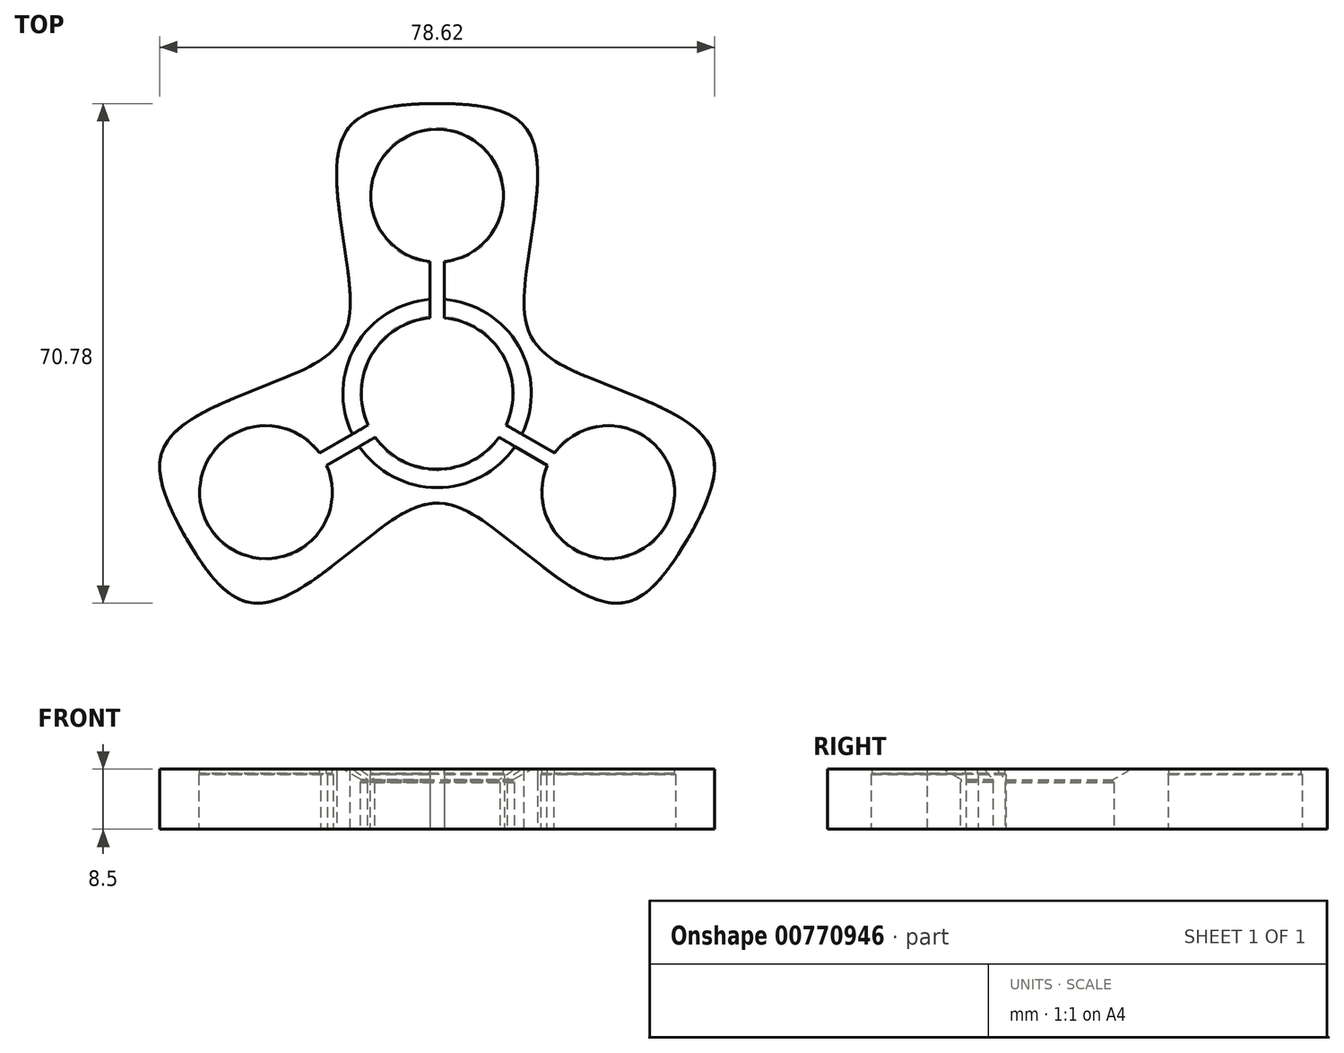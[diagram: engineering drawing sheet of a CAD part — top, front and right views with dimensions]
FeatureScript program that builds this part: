
annotation { "Feature Type Name" : "Feature", "Feature Type Description" : "" }
export const myFeature = defineFeature(function(context is Context, id is Id, definition is map)
    precondition{}
    {
        {
            var Q0;
            Q0=qCreatedBy(makeId("Top.planeOp"),FACE);
            var sketch = newSketch(context, id + "F0", { "sketchPlane" : qUnion([Q0])});
            skLineSegment(sketch, "E0", {"start": v(0, 0) * mm, "end": v(71.1, 41.05) * mm, "construction": true});
            skLineSegment(sketch, "E1", {"start": v(0, 0) * mm, "end": v(-71.1, 41.05) * mm, "construction": true});
            skCircle(sketch, "E2", {"center": v(0, 0) * mm, "radius": 10.9 * mm, "construction": true});
            skCircle(sketch, "E3", {"center": v(0, 28) * mm, "radius": 9.55 * mm});
            skLineSegment(sketch, "E4", {"start": v(-16, 41.05) * mm, "end": v(16, 41.05) * mm});
            skLineSegment(sketch, "E5", {"start": v(16, 41.05) * mm, "end": v(11.13, 6.43) * mm});
            skLineSegment(sketch, "E6", {"start": v(-16, 41.05) * mm, "end": v(-11.13, 6.43) * mm});
            skLineSegment(sketch, "E7", {"start": v(0, 28) * mm, "end": v(0, 41.05) * mm, "construction": true});
            skPoint(sketch, "E8", {"position": v(0, 37.55) * mm});
            skArc(sketch, "E9", {"start": v(9.44, 5.45) * mm, "mid": v(0, 10.9) * mm, "end": v(-9.44, 5.45) * mm});
            skLineSegment(sketch, "E10", {"start": v(-9.44, 5.45) * mm, "end": v(-11.13, 6.43) * mm});
            skLineSegment(sketch, "E11", {"start": v(9.44, 5.45) * mm, "end": v(11.13, 6.43) * mm});
            skSolve(sketch);
        }
        {
            var Q0;
            Q0=qSketchRegion(id+"F0",true);
            extrude(context, id + "F1", {"entities" : qUnion([Q0]), "endBound" : BoundingType.SYMMETRIC, "depth" : 7 * mm, "offsetDistance" : 25 * mm});
        }
        {
            var Q0;
            Q0=makeQuery(id+"F1.opExtrude","SWEPT_EDGE",EDGE,{"disambiguationData":[OSD([sQuery(id+"F0.wireOp",EDGE,"E4"),sQuery(id+"F0.wireOp",EDGE,"E6")])]});
            var Q1;
            Q1=makeQuery(id+"F1.opExtrude","SWEPT_EDGE",EDGE,{"disambiguationData":[OSD([sQuery(id+"F0.wireOp",EDGE,"E4"),sQuery(id+"F0.wireOp",EDGE,"E5")])]});
            fillet(context, id + "F2", {"entities" : qUnion([Q0, Q1]), "radius" : 14 * mm, "tangentPropagation" : true, "rho" : .6, "crossSection" : FilletCrossSection.CONIC, "allowEdgeOverflow" : false});
        }
        {
            var Q0;
            Q0=makeQuery(id+"F1.opExtrude","CAP_FACE",FACE,{"disambiguationData":[OSD([sQuery(id+"F0.wireOp",EDGE,"E3"),sQuery(id+"F0.wireOp",EDGE,"E4"),sQuery(id+"F0.wireOp",EDGE,"E5"),sQuery(id+"F0.wireOp",EDGE,"E6"),sQuery(id+"F0.wireOp",EDGE,"E9"),sQuery(id+"F0.wireOp",EDGE,"E10"),sQuery(id+"F0.wireOp",EDGE,"E11")])],"isStart":false});
            var sketch = newSketch(context, id + "F3", { "sketchPlane" : qUnion([Q0])});
            skCircle(sketch, "E12.0", {"center": v(0, 28) * mm, "radius": 9.55 * mm});
            skCircle(sketch, "E13.0", {"center": v(0, 28) * mm, "radius": 9.4 * mm});
            skArc(sketch, "E14.0", {"start": v(9.44, 5.45) * mm, "mid": v(0, 10.9) * mm, "end": v(-9.44, 5.45) * mm});
            skArc(sketch, "E15.0", {"start": v(9.3, 5.37) * mm, "mid": v(0, 10.75) * mm, "end": v(-9.3, 5.37) * mm});
            skLineSegment(sketch, "E16", {"start": v(-9.3, 5.37) * mm, "end": v(-9.44, 5.45) * mm});
            skLineSegment(sketch, "E17", {"start": v(9.3, 5.37) * mm, "end": v(9.44, 5.45) * mm});
            skSolve(sketch);
        }
        {
            var Q0;
            Q0=makeQuery(id+"F3.imprint","IMPRINT",FACE,{"disambiguationData":[TD([[makeQuery(id+"F3.imprint","IMPRINT",EDGE,{"derivedFrom":sQuery(id+"F3.wireOp",EDGE,"E14.0")}),1.0]])]});
            extrude(context, id + "F4", {"entities" : qUnion([Q0]), "operationType" : NewBodyOperationType.ADD, "oppositeDirection" : true, "depth" : .4 * mm, "offsetDistance" : 25 * mm});
        }
        {
            var Q0;
            Q0=makeQuery(id+"F4.boolean.opBoolean","MERGE",FACE,{"derivedFrom":[makeQuery(id+"F1.opExtrude","CAP_FACE",FACE,{"disambiguationData":[OSD([sQuery(id+"F0.wireOp",EDGE,"E3"),sQuery(id+"F0.wireOp",EDGE,"E4"),sQuery(id+"F0.wireOp",EDGE,"E5"),sQuery(id+"F0.wireOp",EDGE,"E6"),sQuery(id+"F0.wireOp",EDGE,"E9"),sQuery(id+"F0.wireOp",EDGE,"E10"),sQuery(id+"F0.wireOp",EDGE,"E11")])],"isStart":false}),makeQuery(id+"F4.opExtrude","CAP_FACE",FACE,{"disambiguationData":[OSD([sQuery(id+"F3.wireOp",EDGE,"E14.0"),sQuery(id+"F3.wireOp",EDGE,"E15.0"),sQuery(id+"F3.wireOp",EDGE,"E16"),sQuery(id+"F3.wireOp",EDGE,"E17")])],"isStart":true})]});
            extrude(context, id + "F5", {"entities" : qUnion([Q0]), "operationType" : NewBodyOperationType.ADD, "depth" : 1.5 * mm, "offsetDistance" : 25 * mm});
        }
        {
            var Q0;
            Q0=makeQuery(id+"F5.opExtrude","CAP_FACE",FACE,{"disambiguationData":[OSD([sQuery(id+"F0.wireOp",EDGE,"E3"),sQuery(id+"F0.wireOp",EDGE,"E4"),sQuery(id+"F0.wireOp",EDGE,"E5"),sQuery(id+"F0.wireOp",EDGE,"E6"),sQuery(id+"F0.wireOp",EDGE,"E9"),sQuery(id+"F0.wireOp",EDGE,"E10"),sQuery(id+"F0.wireOp",EDGE,"E11"),sQuery(id+"F3.wireOp",EDGE,"E14.0"),sQuery(id+"F3.wireOp",EDGE,"E15.0"),sQuery(id+"F3.wireOp",EDGE,"E16"),sQuery(id+"F3.wireOp",EDGE,"E17")])],"isStart":false});
            var sketch = newSketch(context, id + "F6", { "sketchPlane" : qUnion([Q0])});
            skCircle(sketch, "E18.0", {"center": v(0, 28) * mm, "radius": 9.4 * mm});
            skCircle(sketch, "E19.0", {"center": v(0, 28) * mm, "radius": 9.55 * mm});
            skSolve(sketch);
        }
        {
            var Q0;
            Q0 = qSketchRegion(id + "F6", true);
            extrude(context, id + "F7", {"entities" : qUnion([Q0]), "operationType" : NewBodyOperationType.ADD, "oppositeDirection" : true, "depth" : .75 * mm, "offsetDistance" : 25 * mm});
        }
        {
            var Q0;
            Q0=makeQuery(id+"F4.opExtrude","CAP_EDGE",EDGE,{"disambiguationData":[OSD([sQuery(id+"F3.wireOp",EDGE,"E13.0")])],"isStart":false});
            var Q1;
            Q1=makeQuery(id+"F4.opExtrude","CAP_EDGE",EDGE,{"disambiguationData":[OSD([sQuery(id+"F3.wireOp",EDGE,"E15.0")])],"isStart":false});
            var Q2;
            Q2=makeQuery(id+"F7.opExtrude","CAP_EDGE",EDGE,{"disambiguationData":[OSD([sQuery(id+"F6.wireOp",EDGE,"E18.0")])],"isStart":false});
            chamfer(context, id + "F8", {"entities" : qUnion([Q0, Q1, Q2]), "width" : .15 * mm, "tangentPropagation" : true});
        }
        {
            var Q0;
            Q0=makeQuery(id+"F5.opExtrude","CAP_EDGE",EDGE,{"disambiguationData":[OSD([sQuery(id+"F3.wireOp",EDGE,"E15.0")])],"isStart":false});
            chamfer(context, id + "F9", {"entities" : qUnion([Q0]), "chamferType" : ChamferType.OFFSET_ANGLE, "width" : 1.5 * mm, "oppositeDirection" : false, "angle" : 60 * degree, "tangentPropagation" : true});
        }
        {
            var Q0;
            Q0=qCreatedBy(makeId("Top.planeOp"),FACE);
            var sketch = newSketch(context, id + "F10", { "sketchPlane" : qUnion([Q0])});
            skLineSegment(sketch, "E20.bottom", {"start": v(-1, 0) * mm, "end": v(1, 0) * mm});
            skLineSegment(sketch, "E20.top", {"start": v(-1, 28) * mm, "end": v(1, 28) * mm});
            skLineSegment(sketch, "E20.left", {"start": v(-1, 0) * mm, "end": v(-1, 28) * mm});
            skLineSegment(sketch, "E20.right", {"start": v(1, 0) * mm, "end": v(1, 28) * mm});
            skPoint(sketch, "E21", {"position": v(0, 28) * mm});
            skSolve(sketch);
        }
        {
            var Q0;
            Q0=makeQuery(id+"F10.imprint","IMPRINT",FACE,{"disambiguationData":[TD([[makeQuery(id+"F10.imprint","IMPRINT",EDGE,{"derivedFrom":sQuery(id+"F10.wireOp",EDGE,"E20.bottom")}),1.0]])]});
            extrude(context, id + "F11", {"entities" : qUnion([Q0]), "operationType" : NewBodyOperationType.REMOVE, "endBound" : BoundingType.THROUGH_ALL, "depth" : 25 * mm, "offsetDistance" : 25 * mm, "hasSecondDirection" : true, "secondDirectionBound" : SecondDirectionBoundingType.THROUGH_ALL, "secondDirectionOppositeDirection" : true, "secondDirectionDepth" : 25 * mm});
        }
        {
            var Q0;
            Q0=qCreatedBy(makeId("Front.planeOp"),FACE);
            var sketch = newSketch(context, id + "F12", { "sketchPlane" : qUnion([Q0])});
            skLineSegment(sketch, "E22", {"start": v(0, 0) * mm, "end": v(0, 20.55) * mm, "construction": true});
            skSolve(sketch);
        }
        {
            var Q0;
            Q0=makeQuery(id+"F1.opExtrude","SWEPT_BODY",BODY,{"disambiguationData":[OSD([sQuery(id+"F0.wireOp",EDGE,"E3"),sQuery(id+"F0.wireOp",EDGE,"E4"),sQuery(id+"F0.wireOp",EDGE,"E5"),sQuery(id+"F0.wireOp",EDGE,"E6"),sQuery(id+"F0.wireOp",EDGE,"E9"),sQuery(id+"F0.wireOp",EDGE,"E10"),sQuery(id+"F0.wireOp",EDGE,"E11")])]});
            var Q1;
            Q1=sQuery(id+"F12.wireOp",EDGE,"E22");
            circularPattern(context, id + "F13", {"operationType" : NewBodyOperationType.ADD, "entities" : qUnion([Q0]), "axis" : qUnion([Q1]), "angle" : 360 * degree, "instanceCount" : 3, "equalSpace" : true});
        }
        {
            var Q0;
            Q0=makeQuery(id+"F13.boolean.opBoolean","MERGE",EDGE,{"derivedFrom":[makeQuery(id+"F1.opExtrude","SWEPT_EDGE",EDGE,{"disambiguationData":[OSD([sQuery(id+"F0.wireOp",EDGE,"E5"),sQuery(id+"F0.wireOp",EDGE,"E11")])]}),makeQuery(id+"F13.opPattern","COPY",EDGE,{"derivedFrom":makeQuery(id+"F1.opExtrude","SWEPT_EDGE",EDGE,{"disambiguationData":[OSD([sQuery(id+"F0.wireOp",EDGE,"E6"),sQuery(id+"F0.wireOp",EDGE,"E10")])]}),"instanceName":"2"})]});
            var Q1;
            Q1=makeQuery(id+"F13.boolean.opBoolean","MERGE",EDGE,{"derivedFrom":[makeQuery(id+"F1.opExtrude","SWEPT_EDGE",EDGE,{"disambiguationData":[OSD([sQuery(id+"F0.wireOp",EDGE,"E6"),sQuery(id+"F0.wireOp",EDGE,"E10")])]}),makeQuery(id+"F13.opPattern","COPY",EDGE,{"derivedFrom":makeQuery(id+"F1.opExtrude","SWEPT_EDGE",EDGE,{"disambiguationData":[OSD([sQuery(id+"F0.wireOp",EDGE,"E5"),sQuery(id+"F0.wireOp",EDGE,"E11")])]}),"instanceName":"1"})]});
            var Q2;
            Q2=makeQuery(id+"F13.boolean.opBoolean","MERGE",EDGE,{"derivedFrom":[makeQuery(id+"F13.opPattern","COPY",EDGE,{"derivedFrom":makeQuery(id+"F1.opExtrude","SWEPT_EDGE",EDGE,{"disambiguationData":[OSD([sQuery(id+"F0.wireOp",EDGE,"E6"),sQuery(id+"F0.wireOp",EDGE,"E10")])]}),"instanceName":"1"}),makeQuery(id+"F13.opPattern","COPY",EDGE,{"derivedFrom":makeQuery(id+"F1.opExtrude","SWEPT_EDGE",EDGE,{"disambiguationData":[OSD([sQuery(id+"F0.wireOp",EDGE,"E5"),sQuery(id+"F0.wireOp",EDGE,"E11")])]}),"instanceName":"2"})]});
            fillet(context, id + "F14", {"entities" : qUnion([Q0, Q1, Q2]), "radius" : 14 * mm, "tangentPropagation" : true, "rho" : .6, "crossSection" : FilletCrossSection.CONIC, "allowEdgeOverflow" : false});
        }
    });
